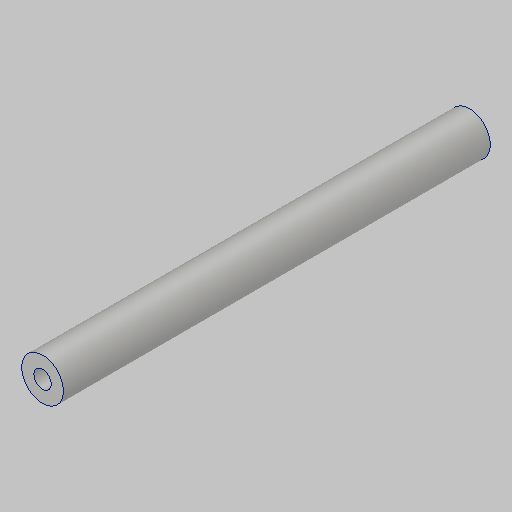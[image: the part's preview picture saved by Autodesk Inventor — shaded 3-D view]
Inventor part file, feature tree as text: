
AUTODESK INVENTOR PART (.ipt)
format: ipt  version: 2023.5 (Build 275446000, 446)  size: 105,472 bytes
history: native  units: in
note: dims shown in document units (in); Inventor stores cm internally (conversion verified against a paired STEP export)
features: extrude x1, hole x1
ambient origin geometry x8: Origin, YZ Plane, XZ Plane, XY Plane, X Axis, Y Axis, Z Axis, Center Point
bodies: Solid1 (feature_tree)
feature tree (2):
  extrude  "Extrusion1"  Depth=3.812in
  hole  "Hole1"  [1 undecoded]
note: 1 required parameter value undecoded (feature->parameter linkage not recoverable at this tier; creation-order binding heuristic only, values carry confidence <= 0.55)
